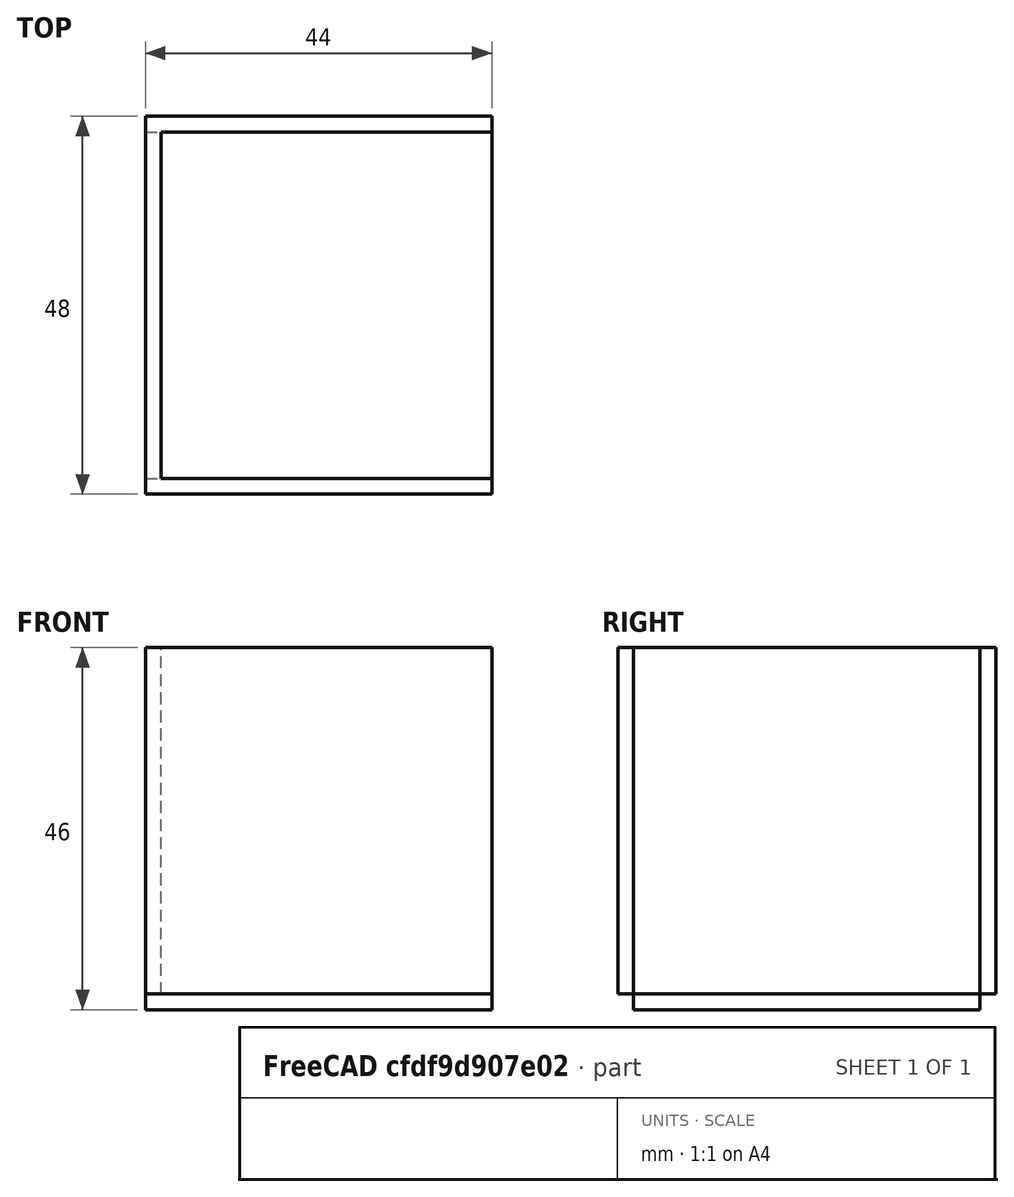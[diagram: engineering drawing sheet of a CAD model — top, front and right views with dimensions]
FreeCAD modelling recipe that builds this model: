
FCSTD DOCUMENT  (FreeCAD 0.20R29410 (Git))
Label: caja
License: All rights reserved
LicenseURL: http://en.wikipedia.org/wiki/All_rights_reserved
objects: Part::Box×4, Part::MultiFuse×1
note: 5 computed .brp shape members not serialized (recipe doc carries the construction recipe); baked Part::Feature solids carry a one-line shape summary decoded from their .brp

FEATURE [Part::Box] Box  label="Cubo"
  AttacherType = Attacher::AttachEngine3D
  Height = 44
  Length = 2
  Width = 44
FEATURE [Part::Box] Box001  label="Cubo001"
  AttacherType = Attacher::AttachEngine3D
  Height = 44
  Length = 2
  Placement = pos=(0,0,0) rot=(0,0,-1;1.5708rad)
  Width = 44
FEATURE [Part::Box] Box002  label="Cubo002"
  AttacherType = Attacher::AttachEngine3D
  Height = 44
  Length = 2
  Placement = pos=(0,46,0) rot=(0,0,-1;1.5708rad)
  Width = 44
FEATURE [Part::Box] Box003  label="Cubo003"
  AttacherType = Attacher::AttachEngine3D
  Height = 44
  Length = 2
  Placement = pos=(0,0,0) rot=(0,1,0;1.5708rad)
  Width = 44
FEATURE [Part::MultiFuse] Fusion
  Shapes = -> [Box,Box001,Box002,Box003]
